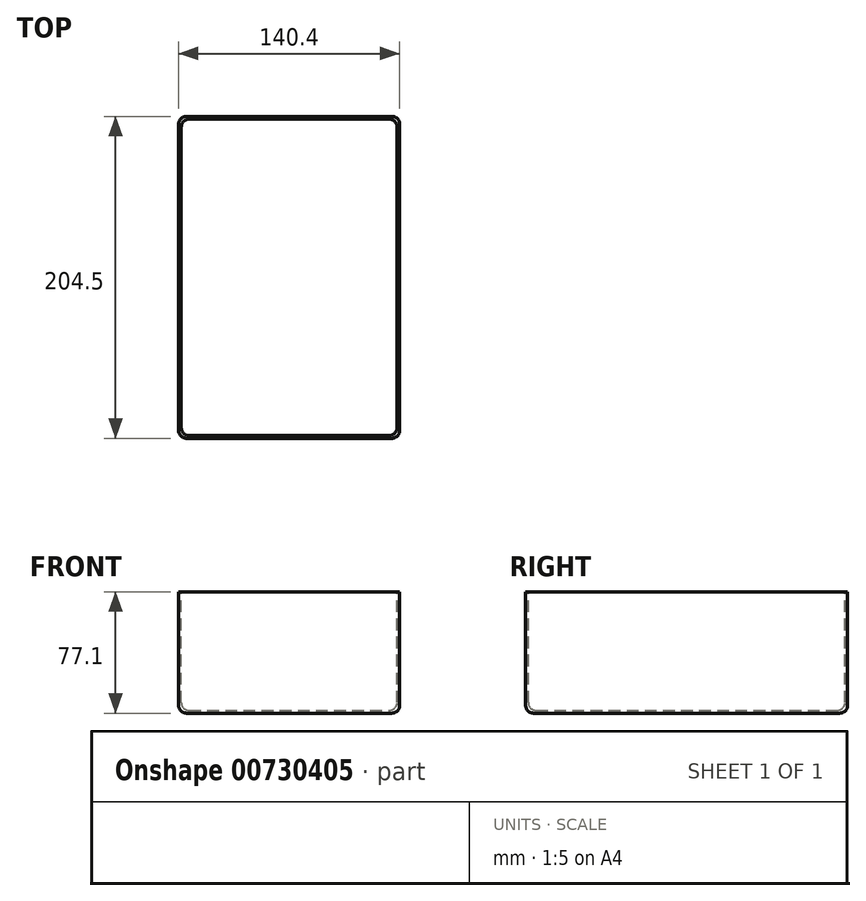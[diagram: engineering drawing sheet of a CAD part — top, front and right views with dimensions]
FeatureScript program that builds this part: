
annotation { "Feature Type Name" : "Feature", "Feature Type Description" : "" }
export const myFeature = defineFeature(function(context is Context, id is Id, definition is map)
    precondition{}
    {
        {
            var Q0;
            Q0=qCreatedBy(makeId("Top.planeOp"),FACE);
            var sketch = newSketch(context, id + "F0", { "sketchPlane" : qUnion([Q0])});
            skLineSegment(sketch, "E0.bottom", {"start": v(0, 0) * mm, "end": v(140.4, 0) * mm});
            skLineSegment(sketch, "E0.top", {"start": v(0, 204.5) * mm, "end": v(140.4, 204.5) * mm});
            skLineSegment(sketch, "E0.left", {"start": v(0, 0) * mm, "end": v(0, 204.5) * mm});
            skLineSegment(sketch, "E0.right", {"start": v(140.4, 0) * mm, "end": v(140.4, 204.5) * mm});
            skSolve(sketch);
        }
        {
            var Q0;
            Q0 = qSketchRegion(id + "F0", true);
            extrude(context, id + "F1", {"entities" : qUnion([Q0]), "depth" : 77.1 * mm, "offsetDistance" : 25 * mm});
        }
        {
            var Q0;
            Q0=makeQuery(id+"F1.opExtrude","CAP_FACE",FACE,{"disambiguationData":[OSD([sQuery(id+"F0.wireOp",EDGE,"E0.bottom"),sQuery(id+"F0.wireOp",EDGE,"E0.top"),sQuery(id+"F0.wireOp",EDGE,"E0.left"),sQuery(id+"F0.wireOp",EDGE,"E0.right")])],"isStart":false});
            var sketch = newSketch(context, id + "F2", { "sketchPlane" : qUnion([Q0])});
            skLineSegment(sketch, "E1.0", {"start": v(1.7, 202.8) * mm, "end": v(138.7, 202.8) * mm});
            skLineSegment(sketch, "E1.1", {"start": v(1.7, 1.7) * mm, "end": v(1.7, 202.8) * mm});
            skLineSegment(sketch, "E1.2", {"start": v(1.7, 1.7) * mm, "end": v(138.7, 1.7) * mm});
            skLineSegment(sketch, "E1.3", {"start": v(138.7, 1.7) * mm, "end": v(138.7, 202.8) * mm});
            skSolve(sketch);
        }
        {
            var Q0;
            Q0 = qSketchRegion(id + "F2", true);
            extrude(context, id + "F3", {"entities" : qUnion([Q0]), "operationType" : NewBodyOperationType.REMOVE, "oppositeDirection" : true, "depth" : (77.1 - 1.7) * mm, "offsetDistance" : 25 * mm});
        }
        {
            var Q0;
            Q0=makeQuery(id+"F3.boolean.opBoolean","COPY",FACE,{"derivedFrom":makeQuery(id+"F3.opExtrude","CAP_FACE",FACE,{"disambiguationData":[OSD([sQuery(id+"F2.wireOp",EDGE,"E1.0"),sQuery(id+"F2.wireOp",EDGE,"E1.1"),sQuery(id+"F2.wireOp",EDGE,"E1.2"),sQuery(id+"F2.wireOp",EDGE,"E1.3")])],"isStart":false})});
            var Q1;
            Q1=makeQuery(id+"F1.opExtrude","CAP_FACE",FACE,{"disambiguationData":[OSD([sQuery(id+"F0.wireOp",EDGE,"E0.bottom"),sQuery(id+"F0.wireOp",EDGE,"E0.top"),sQuery(id+"F0.wireOp",EDGE,"E0.left"),sQuery(id+"F0.wireOp",EDGE,"E0.right")])],"isStart":true});
            fillet(context, id + "F4", {"entities" : qUnion([Q0, Q1]), "radius" : 5 * mm, "tangentPropagation" : true, "allowEdgeOverflow" : false});
        }
        {
            var Q0;
            Q0=makeQuery(id+"F1.opExtrude","SWEPT_EDGE",EDGE,{"disambiguationData":[OSD([sQuery(id+"F0.wireOp",EDGE,"E0.bottom"),sQuery(id+"F0.wireOp",EDGE,"E0.left")])]});
            var Q1;
            Q1=makeQuery(id+"F3.boolean.opBoolean","COPY",EDGE,{"derivedFrom":makeQuery(id+"F3.opExtrude","SWEPT_EDGE",EDGE,{"disambiguationData":[OSD([sQuery(id+"F2.wireOp",EDGE,"E1.0"),sQuery(id+"F2.wireOp",EDGE,"E1.3")])]})});
            var Q2;
            Q2=makeQuery(id+"F1.opExtrude","SWEPT_EDGE",EDGE,{"disambiguationData":[OSD([sQuery(id+"F0.wireOp",EDGE,"E0.bottom"),sQuery(id+"F0.wireOp",EDGE,"E0.right")])]});
            var Q3;
            Q3=makeQuery(id+"F3.boolean.opBoolean","COPY",EDGE,{"derivedFrom":makeQuery(id+"F3.opExtrude","SWEPT_EDGE",EDGE,{"disambiguationData":[OSD([sQuery(id+"F2.wireOp",EDGE,"E1.0"),sQuery(id+"F2.wireOp",EDGE,"E1.1")])]})});
            var Q4;
            Q4=makeQuery(id+"F3.boolean.opBoolean","COPY",EDGE,{"derivedFrom":makeQuery(id+"F3.opExtrude","SWEPT_EDGE",EDGE,{"disambiguationData":[OSD([sQuery(id+"F2.wireOp",EDGE,"E1.1"),sQuery(id+"F2.wireOp",EDGE,"E1.2")])]})});
            var Q5;
            Q5=makeQuery(id+"F1.opExtrude","SWEPT_EDGE",EDGE,{"disambiguationData":[OSD([sQuery(id+"F0.wireOp",EDGE,"E0.top"),sQuery(id+"F0.wireOp",EDGE,"E0.right")])]});
            var Q6;
            Q6=makeQuery(id+"F3.boolean.opBoolean","COPY",EDGE,{"derivedFrom":makeQuery(id+"F3.opExtrude","SWEPT_EDGE",EDGE,{"disambiguationData":[OSD([sQuery(id+"F2.wireOp",EDGE,"E1.2"),sQuery(id+"F2.wireOp",EDGE,"E1.3")])]})});
            var Q7;
            Q7=makeQuery(id+"F1.opExtrude","SWEPT_EDGE",EDGE,{"disambiguationData":[OSD([sQuery(id+"F0.wireOp",EDGE,"E0.top"),sQuery(id+"F0.wireOp",EDGE,"E0.left")])]});
            fillet(context, id + "F5", {"entities" : qUnion([Q0, Q1, Q2, Q3, Q4, Q5, Q6, Q7]), "radius" : 5 * mm, "tangentPropagation" : true, "allowEdgeOverflow" : false});
        }
    });
